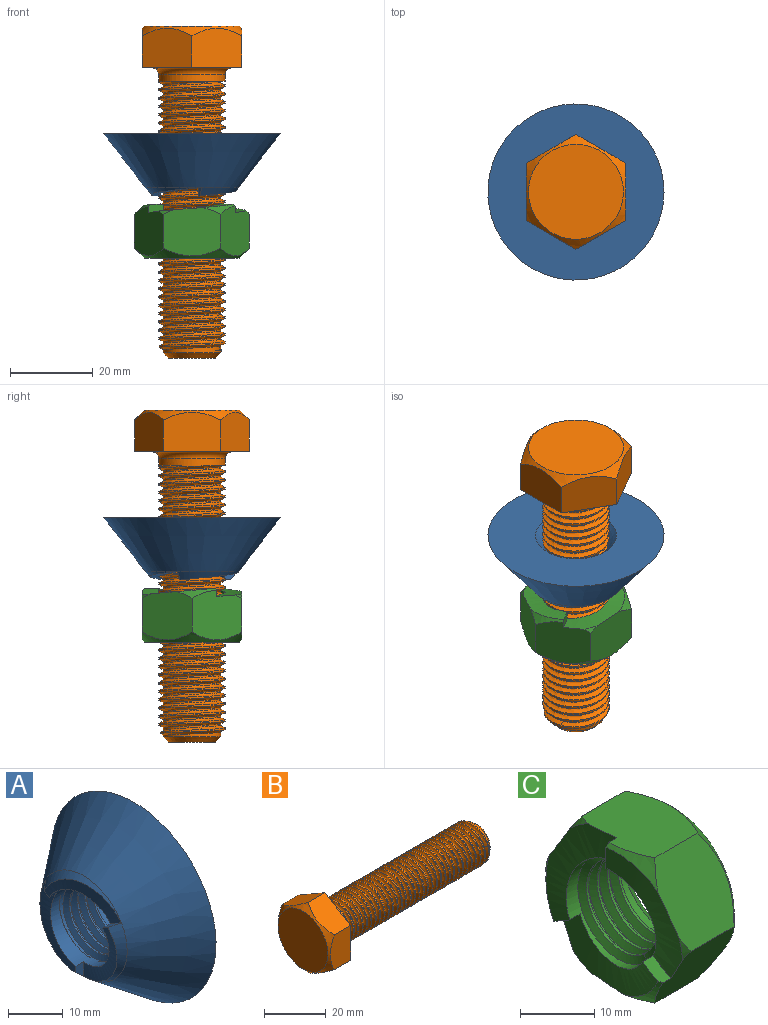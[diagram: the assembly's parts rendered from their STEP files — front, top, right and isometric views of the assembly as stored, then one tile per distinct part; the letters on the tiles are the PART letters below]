
ASSEMBLY  parts=3 mates=3
PART A: 39 faces, bbox 16x42.5x42.5 mm
  f0: bspline ~9.74x7.25mm, area 0mm2, adj f2,f11,f13
  f1: plane 0.02x0.02mm, normal (0,-0.5,-0.87), area 0mm2, adj f2,f10,f18
  f2: cylinder r=8mm len=16mm, axis (-1,0,0), area 174.7mm2, adj f0,f1,f6,f8,f9,f10,f11,f12
  f3: cylinder r=8mm len=16mm, axis (-1,0,0), area 38.5mm2, adj f4,f7,f20,f21,f22,f26,f28,f30
  f4: cylinder r=8mm len=16mm, axis (-1,0,0), area 19.9mm2, adj f3,f5,f26,f28
  f5: cylinder r=8mm len=16mm, axis (-1,0,0), area 20.1mm2, adj f4,f6,f26,f28
  f6: cylinder r=8mm len=16mm, axis (-1,0,0), area 20.5mm2, adj f2,f5,f23,f26,f28
  f7: cylinder r=8mm len=6.34mm, axis (-1,0,0), area 1.1mm2, adj f3,f28,f30
  f8: bspline ~22.73x16.88mm, area 46.2mm2, adj f2,f9,f17,f38
  f9: plane 2.81x2mm, normal (0,0.5,-0.87), area 4.8mm2, adj f2,f8,f33,f38
  f10: cone r=8.88mm half-angle=45deg, axis (-1,0,0), area 0.4mm2, adj f1,f2,f14,f18
  f11: plane 12.56x4.02mm, normal (1,0,0), area 0.3mm2, adj f0,f2,f13,f35
  f12: plane 10.03x8.02mm, normal (1,0,0), area 0.3mm2, adj f2,f15,f29,f34
  f13: cone r=8.88mm half-angle=45deg, axis (-1,0,0), area 0.4mm2, adj f0,f2,f11,f35
  f14: bspline ~9.74x7.25mm, area 0mm2, adj f2,f10,f18
  f15: plane 0.02x0.02mm, normal (0,1,0), area 0mm2, adj f2,f12,f29
  f16: bspline ~22.5x12.99mm, area 46.2mm2, adj f2,f17,f32,f37
  f17: plane 2.81x2mm, normal (0,0.5,0.87), area 4.8mm2, adj f2,f8,f16,f37
  f18: plane 11.74x5.88mm, normal (1,0,0), area 0.3mm2, adj f1,f2,f10,f14
  f19: plane 42.5x42.5mm, normal (1,0,0), area 1118.8mm2, adj f30,f31
  f20: bspline ~9.27x9.08mm, area 8.1mm2, adj f3,f21,f28
  f21: bspline ~8.05x7.99mm, area 5.1mm2, adj f3,f20,f22,f27
  f22: bspline ~9.27x9.08mm, area 8.1mm2, adj f3,f21,f26
  f23: bspline ~12.86x3.65mm, area 8.1mm2, adj f6,f25,f28
  f24: bspline ~12.86x3.91mm, area 8.1mm2, adj f2,f25,f26
  f25: bspline ~11.24x2.8mm, area 5.1mm2, adj f2,f23,f24,f27
  f26: bspline ~16x15.98mm, area 225mm2, adj f2,f3,f4,f5,f6,f22,f24,f27
  f27: cylinder r=6.92mm len=13.83mm, axis (-1,0,0), area 66.5mm2, adj f21,f25,f26,f28
  f28: bspline ~16x15.98mm, area 225mm2, adj f3,f4,f5,f6,f7,f20,f23,f27
  f29: cone r=8.88mm half-angle=45deg, axis (-1,0,0), area 0.4mm2, adj f2,f12,f15,f34
  f30: cone r=8.88mm half-angle=45deg, axis (1,0,0), area 139.7mm2, adj f3,f7,f19
  f31: cone r=11.25mm half-angle=37.6deg, axis (1,0,0), area 1674.6mm2, adj f19,f36,f37,f38
  f32: plane 3.25x2mm, normal (0,-1,0), area 4.8mm2, adj f2,f16,f33,f36
  f33: bspline ~22.73x16.88mm, area 46.2mm2, adj f2,f9,f32,f36
  f34: bspline ~11.25x6.06mm, area 0mm2, adj f2,f12,f29
  f35: plane 0.02x0.02mm, normal (0,-0.5,0.87), area 0mm2, adj f2,f11,f13
  f36: cone r=11.25mm half-angle=41.2deg, axis (1,0,0), area 29.7mm2, adj f31,f32,f33
  f37: cone r=11.25mm half-angle=41.2deg, axis (1,0,0), area 29.7mm2, adj f16,f17,f31
  f38: cone r=11.25mm half-angle=41.2deg, axis (1,0,0), area 29.7mm2, adj f8,f9,f31
PART B: 87 faces, bbox 80.8x28.2x28.2 mm
  f0: torus R=9.6mm, axis (-1,0,0), area 135.5mm2, adj f1,f34
  f1: cylinder r=8mm len=16mm, axis (1,0,0), area 98.5mm2, adj f0,f2,f35,f36,f76
  f2: cylinder r=8mm len=16mm, axis (1,0,0), area 20.1mm2, adj f1,f3,f36,f76
  f3: cylinder r=8mm len=16mm, axis (1,0,0), area 20.1mm2, adj f2,f4,f36,f76
  f4: cylinder r=8mm len=16mm, axis (1,0,0), area 20.1mm2, adj f3,f5,f36,f76
  f5: cylinder r=8mm len=16mm, axis (1,0,0), area 20.1mm2, adj f4,f6,f36,f76
  f6: cylinder r=8mm len=16mm, axis (1,0,0), area 20.1mm2, adj f5,f7,f36,f76
  f7: cylinder r=8mm len=16mm, axis (1,0,0), area 20.1mm2, adj f6,f8,f36,f76
  f8: cylinder r=8mm len=16mm, axis (1,0,0), area 20.1mm2, adj f7,f9,f36,f76
  f9: cylinder r=8mm len=16mm, axis (1,0,0), area 20.1mm2, adj f8,f10,f36,f76
  f10: cylinder r=8mm len=16mm, axis (1,0,0), area 20.1mm2, adj f9,f11,f36,f76
  f11: cylinder r=8mm len=16mm, axis (1,0,0), area 20.1mm2, adj f10,f12,f36,f76
  f12: cylinder r=8mm len=16mm, axis (1,0,0), area 20.1mm2, adj f11,f13,f36,f76
  f13: cylinder r=8mm len=16mm, axis (1,0,0), area 20.1mm2, adj f12,f14,f36,f76
  f14: cylinder r=8mm len=16mm, axis (1,0,0), area 20.1mm2, adj f13,f15,f36,f76
  f15: cylinder r=8mm len=16mm, axis (1,0,0), area 20.1mm2, adj f14,f16,f36,f76
  f16: cylinder r=8mm len=16mm, axis (1,0,0), area 20.1mm2, adj f15,f17,f36,f76
  f17: cylinder r=8mm len=16mm, axis (1,0,0), area 20.1mm2, adj f16,f18,f36,f76
  f18: cylinder r=8mm len=16mm, axis (1,0,0), area 20.1mm2, adj f17,f19,f36,f76
  f19: cylinder r=8mm len=16mm, axis (1,0,0), area 20.1mm2, adj f18,f20,f36,f76
  f20: cylinder r=8mm len=16mm, axis (1,0,0), area 20.1mm2, adj f19,f21,f36,f76
  f21: cylinder r=8mm len=16mm, axis (1,0,0), area 20.1mm2, adj f20,f22,f36,f76
  f22: cylinder r=8mm len=16mm, axis (1,0,0), area 20.1mm2, adj f21,f23,f36,f76
  f23: cylinder r=8mm len=16mm, axis (1,0,0), area 20.1mm2, adj f22,f24,f36,f76
  f24: cylinder r=8mm len=16mm, axis (1,0,0), area 20.1mm2, adj f23,f25,f36,f76
  f25: cylinder r=8mm len=16mm, axis (1,0,0), area 20.1mm2, adj f24,f26,f36,f76
  f26: cylinder r=8mm len=16mm, axis (1,0,0), area 20.1mm2, adj f25,f27,f36,f76
  f27: cylinder r=8mm len=16mm, axis (1,0,0), area 20.1mm2, adj f26,f28,f36,f76
  f28: cylinder r=8mm len=16mm, axis (1,0,0), area 20.1mm2, adj f27,f29,f36,f76
  f29: cylinder r=8mm len=16mm, axis (1,0,0), area 20.1mm2, adj f28,f30,f36,f76
  f30: cylinder r=8mm len=16mm, axis (1,0,0), area 20.1mm2, adj f29,f31,f36,f76
  f31: cylinder r=8mm len=16mm, axis (1,0,0), area 20.1mm2, adj f30,f32,f36,f76
  f32: cylinder r=8mm len=16mm, axis (1,0,0), area 20.1mm2, adj f31,f33,f36,f76
  f33: cylinder r=8mm len=4mm, axis (1,0,0), area 2mm2, adj f32,f36,f74,f76
  f34: plane 23x23mm, normal (1,0,0), area 125.9mm2, adj f0,f81
  f35: plane 16.5x16.11mm, normal (1,0,0), area 25.7mm2, adj f1,f36,f38,f76
  f36: bspline ~64.4x15.98mm, area 1843.1mm2, adj f1,f2,f3,f4,f5,f6,f7,f8
  f37: cone r=6.27mm half-angle=45deg, axis (-1,0,0), area 72.4mm2, adj f71,f72
  f38: cylinder r=6.92mm len=7.73mm, axis (1,0,0), area 1.7mm2, adj f35,f36,f39
  f39: cylinder r=6.92mm len=13.84mm, axis (1,0,0), area 17.4mm2, adj f36,f38,f40,f76
  f40: cylinder r=6.92mm len=13.84mm, axis (1,0,0), area 17.4mm2, adj f36,f39,f41,f76
  f41: cylinder r=6.92mm len=13.84mm, axis (1,0,0), area 17.4mm2, adj f36,f40,f42,f76
  f42: cylinder r=6.92mm len=13.84mm, axis (1,0,0), area 17.4mm2, adj f36,f41,f43,f76
  f43: cylinder r=6.92mm len=13.84mm, axis (1,0,0), area 17.4mm2, adj f36,f42,f44,f76
  f44: cylinder r=6.92mm len=13.84mm, axis (1,0,0), area 17.4mm2, adj f36,f43,f45,f76
  f45: cylinder r=6.92mm len=13.84mm, axis (1,0,0), area 17.4mm2, adj f36,f44,f46,f76
  f46: cylinder r=6.92mm len=13.84mm, axis (1,0,0), area 17.4mm2, adj f36,f45,f47,f76
  f47: cylinder r=6.92mm len=13.84mm, axis (1,0,0), area 17.4mm2, adj f36,f46,f48,f76
  f48: cylinder r=6.92mm len=13.84mm, axis (1,0,0), area 17.4mm2, adj f36,f47,f49,f76
  f49: cylinder r=6.92mm len=13.84mm, axis (1,0,0), area 17.4mm2, adj f36,f48,f50,f76
  f50: cylinder r=6.92mm len=13.84mm, axis (1,0,0), area 17.4mm2, adj f36,f49,f51,f76
  f51: cylinder r=6.92mm len=13.84mm, axis (1,0,0), area 17.4mm2, adj f36,f50,f52,f76
  f52: cylinder r=6.92mm len=13.84mm, axis (1,0,0), area 17.4mm2, adj f36,f51,f53,f76
  f53: cylinder r=6.92mm len=13.84mm, axis (1,0,0), area 17.4mm2, adj f36,f52,f54,f76
  f54: cylinder r=6.92mm len=13.84mm, axis (1,0,0), area 17.4mm2, adj f36,f53,f55,f76
  f55: cylinder r=6.92mm len=13.84mm, axis (1,0,0), area 17.4mm2, adj f36,f54,f56,f76
  f56: cylinder r=6.92mm len=13.84mm, axis (1,0,0), area 17.4mm2, adj f36,f55,f57,f76
  f57: cylinder r=6.92mm len=13.84mm, axis (1,0,0), area 17.4mm2, adj f36,f56,f58,f76
  f58: cylinder r=6.92mm len=13.84mm, axis (1,0,0), area 17.4mm2, adj f36,f57,f59,f76
  f59: cylinder r=6.92mm len=13.84mm, axis (1,0,0), area 17.4mm2, adj f36,f58,f60,f76
  f60: cylinder r=6.92mm len=13.84mm, axis (1,0,0), area 17.4mm2, adj f36,f59,f61,f76
  f61: cylinder r=6.92mm len=13.84mm, axis (1,0,0), area 17.4mm2, adj f36,f60,f62,f76
  f62: cylinder r=6.92mm len=13.84mm, axis (1,0,0), area 17.3mm2, adj f36,f61,f63,f76
  f63: cylinder r=6.92mm len=13.84mm, axis (1,0,0), area 17.4mm2, adj f36,f62,f64,f76
  f64: cylinder r=6.92mm len=13.84mm, axis (1,0,0), area 17.4mm2, adj f36,f63,f65,f76
  f65: cylinder r=6.92mm len=13.84mm, axis (1,0,0), area 17.4mm2, adj f36,f64,f66,f76
  f66: cylinder r=6.92mm len=13.84mm, axis (1,0,0), area 17.4mm2, adj f36,f65,f67,f76
  f67: cylinder r=6.92mm len=13.84mm, axis (1,0,0), area 17.4mm2, adj f36,f66,f68,f76
  f68: cylinder r=6.92mm len=13.84mm, axis (1,0,0), area 17.4mm2, adj f36,f67,f69,f76
  f69: cylinder r=6.92mm len=13.84mm, axis (1,0,0), area 17.4mm2, adj f36,f68,f70,f76
  f70: cylinder r=6.92mm len=13.84mm, axis (1,0,0), area 24.7mm2, adj f36,f69,f71,f73,f76
  f71: cylinder r=6.92mm len=13.84mm, axis (1,0,0), area 28.1mm2, adj f37,f70,f73,f74,f75,f76
  f72: plane 11.24x11.24mm, normal (1,0,0), area 99.1mm2, adj f37
  f73: bspline ~16x12.06mm, area 18.2mm2, adj f36,f70,f71,f74
  f74: bspline ~16x12.06mm, area 12.1mm2, adj f33,f71,f73,f75
  f75: bspline ~16x12.06mm, area 18.2mm2, adj f71,f74,f76
  f76: bspline ~65.4x16mm, area 1871.6mm2, adj f1,f2,f3,f4,f5,f6,f7,f8
  f77: cone r=12.66mm half-angle=45deg, axis (1,0,0), area 122.3mm2, adj f78,f79,f80,f82,f83,f84,f85
  f78: plane 12x10.14mm, normal (0,0.5,0.87), area 120.8mm2, adj f77,f79,f83,f86
  f79: plane 12x10.14mm, normal (0,-0.5,0.87), area 120.8mm2, adj f77,f78,f80,f86
  f80: plane 13.86x10.14mm, normal (0,-1,0), area 120.8mm2, adj f77,f79,f82,f86
  f81: cylinder r=11.5mm len=23mm, axis (1,0,0), area 14.5mm2, adj f34,f86
  f82: plane 12x10.14mm, normal (0,-0.5,-0.87), area 120.8mm2, adj f77,f80,f84,f86
  f83: plane 13.86x10.14mm, normal (0,1,0), area 120.8mm2, adj f77,f78,f84,f86
  f84: plane 12x10.14mm, normal (0,0.5,-0.87), area 120.8mm2, adj f77,f82,f83,f86
  f85: plane 22.91x22.91mm, normal (-1,0,0), area 412.3mm2, adj f77
  f86: plane 27.71x24mm, normal (1,0,0), area 83.4mm2, adj f78,f79,f80,f81,f82,f83,f84
PART C: 32 faces, bbox 14.2x35.6x31 mm
  f0: cylinder r=8mm len=16mm, axis (1,0,0), area 175.1mm2, adj f8,f9,f10,f11,f12,f13,f14,f16
  f1: cone r=12.66mm half-angle=45deg, axis (1,0,0), area 13.4mm2, adj f3,f22,f27,f30
  f2: cone r=12.66mm half-angle=45deg, axis (1,0,0), area 2.4mm2, adj f3,f4,f30
  f3: plane 14.86x13.53mm, normal (0,0,-1), area 145.2mm2, adj f1,f2,f4,f20,f22,f30
  f4: plane 13.54x12.6mm, normal (0,0.87,-0.5), area 142.8mm2, adj f2,f3,f19,f20,f24,f30,f31
  f5: cone r=12.66mm half-angle=45deg, axis (1,0,0), area 2.4mm2, adj f23,f24,f28
  f6: cone r=12.66mm half-angle=45deg, axis (1,0,0), area 13.4mm2, adj f21,f23,f26,f29
  f7: cone r=12.66mm half-angle=45deg, axis (1,0,0), area 2.4mm2, adj f21,f22,f26
  f8: bspline ~9.27x9.08mm, area 8.1mm2, adj f0,f9,f16
  f9: bspline ~8.05x7.99mm, area 5.1mm2, adj f0,f8,f10,f15
  f10: bspline ~9.27x9.08mm, area 8.1mm2, adj f0,f9,f14
  f11: bspline ~12.86x3.65mm, area 8.1mm2, adj f0,f13,f16
  f12: bspline ~12.86x3.91mm, area 8.1mm2, adj f0,f13,f14,f25
  f13: bspline ~11.24x2.8mm, area 5.1mm2, adj f0,f11,f12,f15
  f14: bspline ~16.61x16.54mm, area 224.9mm2, adj f0,f10,f12,f15
  f15: cylinder r=6.92mm len=13.83mm, axis (-1,0,0), area 66.5mm2, adj f9,f13,f14,f16
  f16: bspline ~16.61x16.54mm, area 225mm2, adj f0,f8,f11,f15
  f17: cone r=8.88mm half-angle=45deg, axis (1,0,0), area 139.7mm2, adj f0,f18
  f18: plane 22.91x22.91mm, normal (1,0,0), area 112.5mm2, adj f17,f20
  f19: cone r=12.66mm half-angle=45deg, axis (1,0,0), area 13.4mm2, adj f4,f24,f28,f31
  f20: cone r=12.66mm half-angle=45deg, axis (-1,0,0), area 122.3mm2, adj f3,f4,f18,f21,f22,f23,f24
  f21: plane 13.09x12.56mm, normal (0,-0.87,0.5), area 145.2mm2, adj f6,f7,f20,f22,f23,f26
  f22: plane 13.02x12.09mm, normal (0,-0.87,-0.5), area 142.8mm2, adj f1,f3,f7,f20,f21,f26,f27
  f23: plane 14.46x13.54mm, normal (0,0,1), area 142.8mm2, adj f5,f6,f20,f21,f24,f28,f29
  f24: plane 13.53x13.01mm, normal (0,0.87,0.5), area 145.2mm2, adj f4,f5,f19,f20,f23,f28
  f25: cylinder r=8mm len=0.16mm, axis (1,0,0), area 0mm2, adj f12,f26,f27
  f26: bspline ~30x17.32mm, area 89.2mm2, adj f0,f6,f7,f21,f22,f25,f27,f29
  f27: plane 3.46x2mm, normal (0,-0.5,0.87), area 7.9mm2, adj f0,f1,f22,f25,f26,f30
  f28: bspline ~30.31x22.5mm, area 92.5mm2, adj f0,f5,f19,f23,f24,f29,f31
  f29: plane 4x2mm, normal (0,1,0), area 7.9mm2, adj f0,f6,f23,f26,f28
  f30: bspline ~22.64x9.07mm, area 92.6mm2, adj f0,f1,f2,f3,f4,f27,f31
  f31: plane 3.46x2mm, normal (0,-0.5,-0.87), area 7.9mm2, adj f0,f4,f19,f28,f30
PLACE A rot(axis=(0.7,-0.11,0.7),167.4deg) t=(0,0,-39)mm
PLACE B rot(axis=(0.58,0.58,-0.58),120deg) t=(0,0,0)mm
PLACE C rot(axis=(-0.58,0.58,0.58),120deg) t=(0,0,-43)mm
MATE cylindrical A.f10 <-> B.f37  axis (0,0,1) through (0,0,-26)mm
MATE revolute C.f1 <-> A.f36  axis (0,0,-1) through (0,0,-56)mm
MATE slider B.f1 <-> C.f0  axis (0,0,1) through (0,0,0)mm
